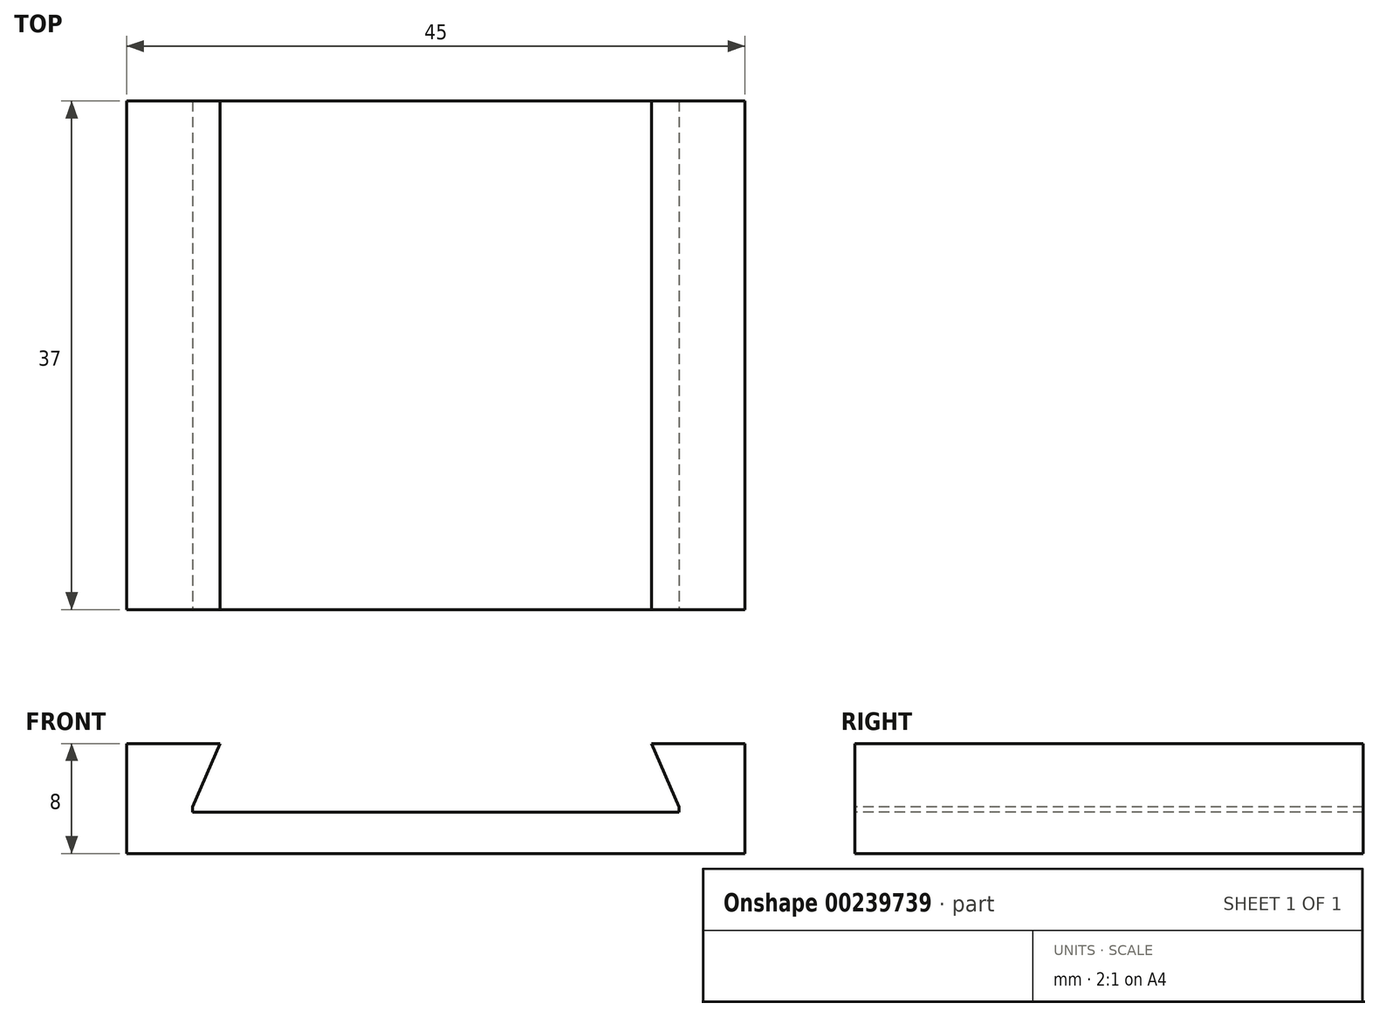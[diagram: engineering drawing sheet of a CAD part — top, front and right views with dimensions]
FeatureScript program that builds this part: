
annotation { "Feature Type Name" : "Feature", "Feature Type Description" : "" }
export const myFeature = defineFeature(function(context is Context, id is Id, definition is map)
    precondition{}
    {
        {
            var Q0;
            Q0=qCreatedBy(makeId("Top.planeOp"),FACE);
            var sketch = newSketch(context, id + "F0", { "sketchPlane" : qUnion([Q0])});
            skLineSegment(sketch, "E0.bottom", {"start": v(22.5, -18.5) * mm, "end": v(-22.5, -18.5) * mm});
            skLineSegment(sketch, "E0.top", {"start": v(22.5, 18.5) * mm, "end": v(-22.5, 18.5) * mm});
            skLineSegment(sketch, "E0.left", {"start": v(22.5, -18.5) * mm, "end": v(22.5, 18.5) * mm});
            skLineSegment(sketch, "E0.right", {"start": v(-22.5, -18.5) * mm, "end": v(-22.5, 18.5) * mm});
            skPoint(sketch, "E0.middle", {"position": v(0, 0) * mm});
            skSolve(sketch);
        }
        {
            var Q0;
            Q0 = qSketchRegion(id + "F0", true);
            extrude(context, id + "F1", {"entities" : qUnion([Q0]), "depth" : 8 * mm});
        }
        {
            var Q0;
            Q0=makeQuery(id+"F1.opExtrude","SWEPT_FACE",FACE,{"disambiguationData":[OSD([sQuery(id+"F0.wireOp",EDGE,"E0.bottom")])]});
            var sketch = newSketch(context, id + "F2", { "sketchPlane" : qUnion([Q0])});
            skLineSegment(sketch, "E1", {"start": v(-22.5, 3) * mm, "end": v(22.5, 3) * mm, "construction": true});
            skLineSegment(sketch, "E2", {"start": v(-17.7, 8) * mm, "end": v(-17.7, 0) * mm, "construction": true});
            skLineSegment(sketch, "E3", {"start": v(0, 13.1) * mm, "end": v(0, -6.27) * mm, "construction": true});
            skLineSegment(sketch, "E4.MirrorCS", {"start": v(17.7, 8) * mm, "end": v(17.7, 0) * mm, "construction": true});
            skLineSegment(sketch, "E5", {"start": v(-15.7, 8) * mm, "end": v(-15.7, 0) * mm, "construction": true});
            skLineSegment(sketch, "E6", {"start": v(-15.7, 8) * mm, "end": v(15.7, 8) * mm});
            skLineSegment(sketch, "E7", {"start": v(-17.7, 3) * mm, "end": v(17.7, 3) * mm});
            skLineSegment(sketch, "E8", {"start": v(-17.7, 3) * mm, "end": v(-17.7, 3.4) * mm});
            skLineSegment(sketch, "E9", {"start": v(-17.7, 3.4) * mm, "end": v(-15.7, 8) * mm});
            skLineSegment(sketch, "E10.MirrorCS", {"start": v(17.7, 3.4) * mm, "end": v(15.7, 8) * mm});
            skLineSegment(sketch, "E11", {"start": v(17.7, 3.4) * mm, "end": v(17.7, 3) * mm});
            skSolve(sketch);
        }
        {
            var Q0;
            Q0 = qSketchRegion(id + "F2", true);
            extrude(context, id + "F3", {"entities" : qUnion([Q0]), "operationType" : NewBodyOperationType.REMOVE, "endBound" : BoundingType.THROUGH_ALL, "oppositeDirection" : true, "depth" : 25 * mm});
        }
    });
